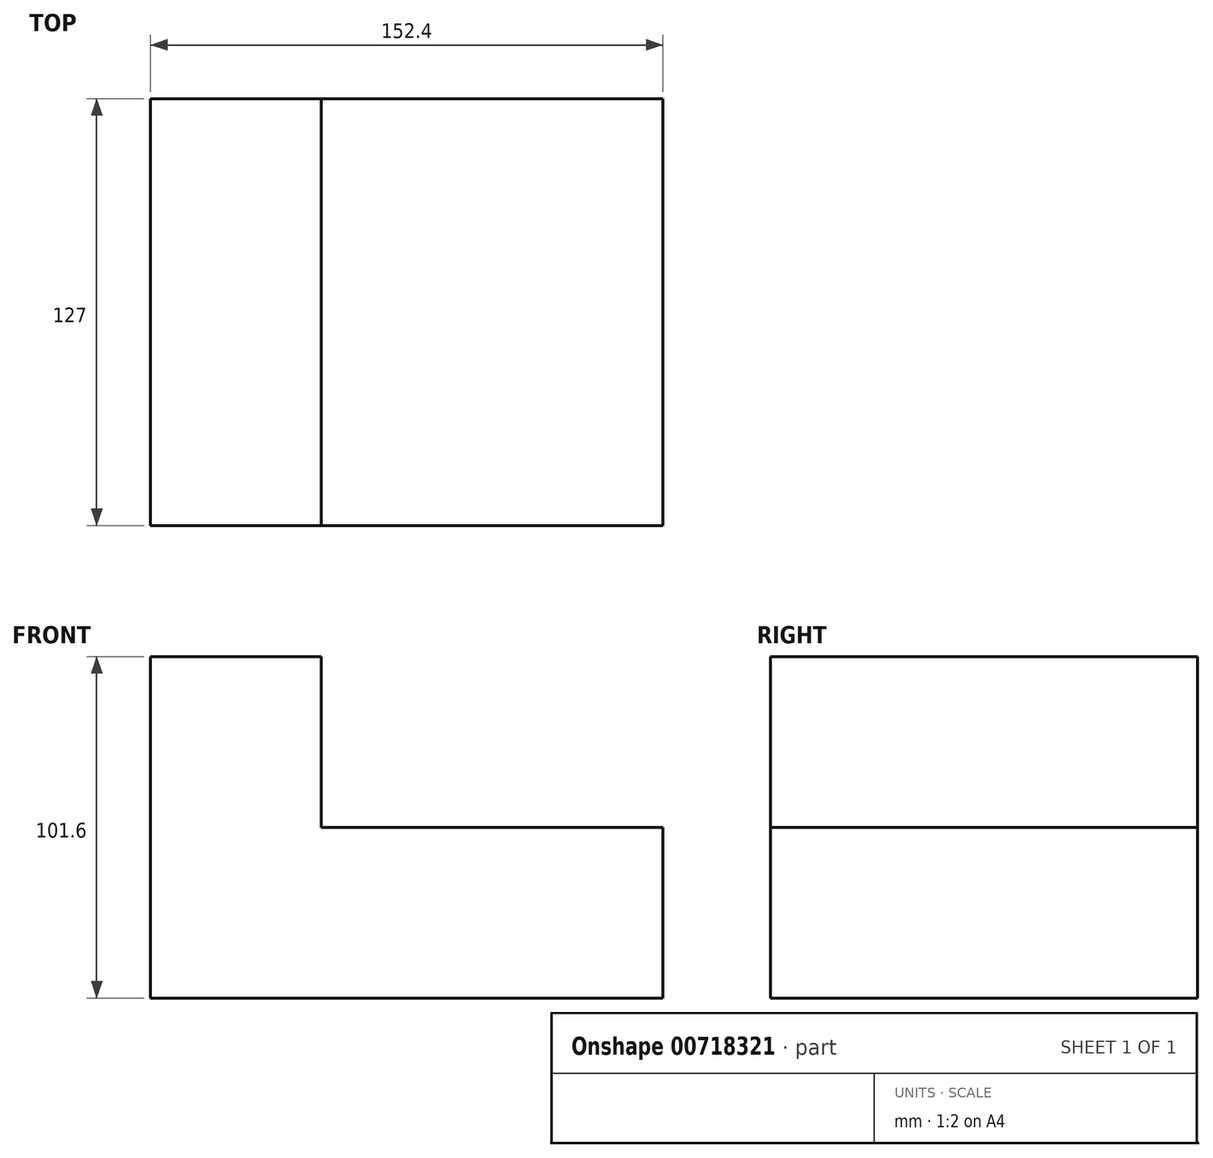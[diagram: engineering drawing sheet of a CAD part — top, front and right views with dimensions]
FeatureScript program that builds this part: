
annotation { "Feature Type Name" : "Feature", "Feature Type Description" : "" }
export const myFeature = defineFeature(function(context is Context, id is Id, definition is map)
    precondition{}
    {
        {
            var Q0;
            Q0=qCreatedBy(makeId("Front.planeOp"),FACE);
            var sketch = newSketch(context, id + "F0", { "sketchPlane" : qUnion([Q0])});
            skLineSegment(sketch, "E0", {"start": v(-110.99, -13.8) * mm, "end": v(-11.97, -13.8) * mm});
            skLineSegment(sketch, "E1", {"start": v(-11.97, -13.8) * mm, "end": v(41.41, -13.8) * mm});
            skLineSegment(sketch, "E2", {"start": v(41.41, -13.8) * mm, "end": v(41.41, 37) * mm});
            skLineSegment(sketch, "E3", {"start": v(41.41, 37) * mm, "end": v(-60.19, 37) * mm});
            skLineSegment(sketch, "E4", {"start": v(-60.19, 37) * mm, "end": v(-60.19, 87.8) * mm});
            skLineSegment(sketch, "E5", {"start": v(-60.19, 87.8) * mm, "end": v(-115.3, 87.8) * mm});
            skLineSegment(sketch, "E6", {"start": v(-115.3, 87.8) * mm, "end": v(-108.98, 87.8) * mm});
            skLineSegment(sketch, "E7", {"start": v(-108.98, 87.8) * mm, "end": v(-110.99, 87.8) * mm});
            skLineSegment(sketch, "E8", {"start": v(-110.99, 87.8) * mm, "end": v(-110.99, -13.8) * mm});
            skSolve(sketch);
        }
        {
            var Q0;
            Q0=makeQuery(id+"F0.imprint","IMPRINT",FACE,{"disambiguationData":[TD([[makeQuery(id+"F0.imprint","IMPRINT",EDGE,{"derivedFrom":sQuery(id+"F0.wireOp",EDGE,"E0")}),1.0]])]});
            extrude(context, id + "F1", {"entities" : qUnion([Q0]), "depth" : 127 * mm, "offsetDistance" : 25.4 * mm});
        }
    });
